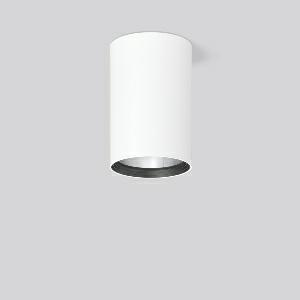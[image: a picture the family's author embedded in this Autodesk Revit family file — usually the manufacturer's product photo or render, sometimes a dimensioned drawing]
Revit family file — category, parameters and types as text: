
# Revit family: heledon_maxi_a_931216_002_1_d42b
name_source: partatom
category: Lighting Fixtures
units: mm (PartAtom-declared; Revit-internal decimal feet)

## family parameters
Cut with Voids When Loaded = No
Host = Face
Light Source = No
Part Type = Normal
Room Calculation Point = No
Round Connector Dimension = Use Diameter
Shared = No

## types (1)
- HELEDON maxi A (1 x LED Modul 940, 3400 lm, 4000)
    Apparent Load = 25 VA
    Approval mark = CE
    CIE Flux Codes = 100 100 100 100 100
    Color Rendering = 92
    Color Temperature = 4000
    Default Elevation = 1800 mm
    Description = Series: HELEDON maxi
Cylindrical surface-mounted downlight. Housing: die-cast aluminium, powder-coated. Internal ceiling frame polycarbonate with bayonet mounting. Black plastic ring and recessed LED to prevent glare from the side. Optical assembly with reflector made of MIRO-Silver with 98% total light reflection for outstanding efficiency - can be changed without tools. Best colour rendering index Ra>90. Suitable for Ceiling mounting. Easy installation with a separate ceiling frame with bayonet mounting and plug connection. Driver integrated. Connected via plug-in connector. High quality converter without flickering and stroboscopic effect. The following accessories can be mounted without use of tools: interchangeable lenses, decorative glasses, honeycomb louvre, clear and frosted diffusers, white interchangeable plastic ring. 
Colour: traffic white, matt (RAL 9016)
Diameter: 123 mm
Height: 183 mm
Lamp: LED
Socket: without socket
Colour temperature: 4000K
Colour rendering index (CRI): 92
System power: 25 W
Rated luminous flux: 3400 lm
Luminous efficiency: 136 lm/W
Control gear: Regulated power supply
Protection class: I
Type of protection: IP 20
    Height = 183 mm
    Lamp = 1 x LED Modul 940
    Lamp Light Flux = 3400 lm
    Lamp count = 1
    Length = 123 mm
    Lifetime = 50000 h
    Luminous efficacy = 136 lm/W
    Manufacturer = RZB
    ModVariant = No
    Model = 931216.002.1
    Mounting Place = Ceiling
    Mounting Type = Surface mounted
    Number of Poles = 1
    OnlyDefault = Yes
    Power Factor = 1
    Product Name = HELEDON maxi A
    Product group = Surface mounted downlights
    ProductGroupID = 302
    Protection Class = Protection class I
    Protection Degree = IP 20
    RLX_Detail_Level = 1
    RLX_Emergency_Light_Flux = 0 lm
    RLX_Emergency_Type = 0
    RLX_Emergency_Type_DB = No
    RlxData = <blob elided: 96621 chars, md5=768a83b2>
    Socket = socket
    Standby Power = 0 W
    System Light Flux = 3400 lm
    System Power = 25 W
    Type Comments = Product without accessories
    Type Image = 931192.002.jpg
    URL = http://relux.com
    VarID = ---
    Voltage = 230 V
    Voltage Range = 220-240 V
    Weight = 0.00 kg
    Width = 0 mm  [stored 0 ft]

note: [stored X ft] marks values corroborated as IEEE doubles in the binary element streams (Revit-internal decimal feet)

## geometry (parser evidence)
native form markers: Blend x4, Sweep x9
no freeform markers — native parametric forms only
